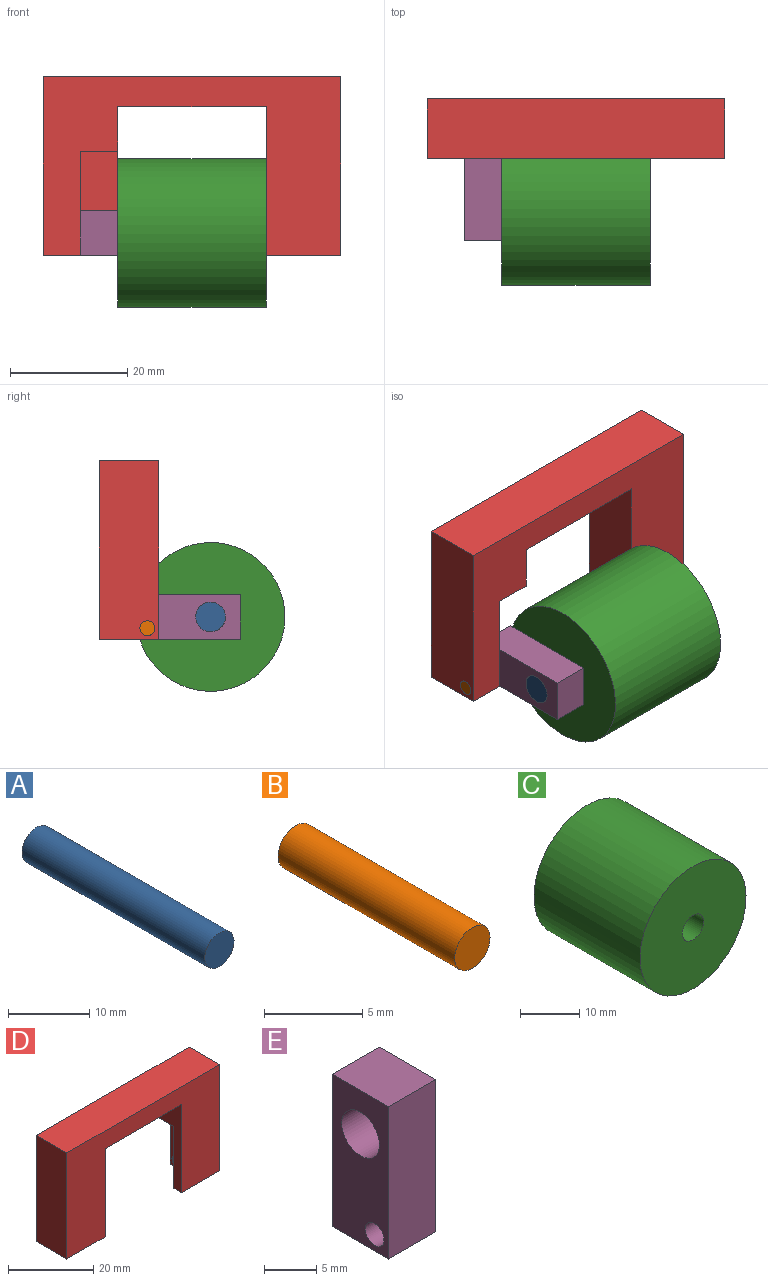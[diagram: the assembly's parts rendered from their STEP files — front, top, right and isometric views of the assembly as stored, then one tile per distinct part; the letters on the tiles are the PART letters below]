
ASSEMBLY  parts=5 mates=4
PART A: 3 faces, bbox 5.1x31.8x5.1 mm
  f0: cylinder r=2.54mm len=31.75mm, axis (0,1,0), area 506.7mm2, adj f1,f2
  f1: plane 5.08x5.08mm, normal (0,-1,0), area 20.3mm2, adj f0
  f2: plane 5.08x5.08mm, normal (0,1,0), area 20.3mm2, adj f0
PART B: 3 faces, bbox 2.5x12.7x2.5 mm
  f0: cylinder r=1.27mm len=12.7mm, axis (0,1,0), area 101.3mm2, adj f1,f2
  f1: plane 2.54x2.54mm, normal (0,-1,0), area 5.1mm2, adj f0
  f2: plane 2.54x2.54mm, normal (0,1,0), area 5.1mm2, adj f0
PART C: 4 faces, bbox 25.4x25.4x25.4 mm
  f0: cylinder r=12.7mm len=25.4mm, axis (0,1,0), area 2026.8mm2, adj f1,f2
  f1: plane 25.4x25.4mm, normal (0,-1,0), area 486.4mm2, adj f0,f3
  f2: plane 25.4x25.4mm, normal (0,1,0), area 486.4mm2, adj f0,f3
  f3: cylinder r=2.54mm len=25.4mm, axis (0,-1,0), area 405.4mm2, adj f1,f2
PART D: 14 faces, bbox 50.8x10.2x30.5 mm
  f0: plane 50.8x30.48mm, normal (0,1,0), area 790.3mm2, adj f1,f2,f3,f4,f5,f6,f7,f8
  f1: plane 25.4x10.16mm, normal (-1,0,0), area 122.6mm2, adj f0,f2,f8,f9,f10,f12
  f2: plane 12.7x10.16mm, normal (0,0,-1), area 80.6mm2, adj f0,f1,f3,f9,f11,f12
  f3: plane 30.48x10.16mm, normal (1,0,0), area 304.6mm2, adj f0,f2,f4,f9,f13
  f4: plane 50.8x10.16mm, normal (0,0,1), area 516.1mm2, adj f0,f3,f5,f9
  f5: plane 30.48x10.16mm, normal (-1,0,0), area 309.7mm2, adj f0,f4,f6,f9
  f6: plane 12.7x10.16mm, normal (0,0,-1), area 129mm2, adj f0,f5,f7,f9
  f7: plane 25.4x10.16mm, normal (1,0,0), area 258.1mm2, adj f0,f6,f8,f9
  f8: plane 25.4x10.16mm, normal (0,0,-1), area 258.1mm2, adj f0,f1,f7,f9
  f9: plane 50.8x30.48mm, normal (0,-1,0), area 903.2mm2, adj f1,f2,f3,f4,f5,f6,f7,f8
  f10: plane 7.62x6.35mm, normal (0,0,-1), area 48.4mm2, adj f0,f1,f11,f12
  f11: plane 17.78x7.62mm, normal (-1,0,0), area 130.4mm2, adj f0,f2,f10,f12,f13
  f12: plane 17.78x6.35mm, normal (0,1,0), area 112.9mm2, adj f1,f2,f10,f11
  f13: cylinder r=1.27mm len=6.35mm, axis (1,0,0), area 50.7mm2, adj f3,f11
PART E: 8 faces, bbox 6.4x7.6x17.8 mm
  f0: plane 17.78x7.62mm, normal (-1,0,0), area 110.1mm2, adj f1,f3,f4,f5,f6,f7
  f1: plane 7.62x6.35mm, normal (0,0,-1), area 48.4mm2, adj f0,f2,f4,f5
  f2: plane 17.78x7.62mm, normal (1,0,0), area 110.1mm2, adj f1,f3,f4,f5,f6,f7
  f3: plane 7.62x6.35mm, normal (0,0,1), area 48.4mm2, adj f0,f2,f4,f5
  f4: plane 17.78x6.35mm, normal (0,1,0), area 112.9mm2, adj f0,f1,f2,f3
  f5: plane 17.78x6.35mm, normal (0,-1,0), area 112.9mm2, adj f0,f1,f2,f3
  f6: cylinder r=1.27mm len=6.35mm, axis (1,0,0), area 50.7mm2, adj f0,f2
  f7: cylinder r=2.54mm len=6.35mm, axis (1,0,0), area 101.3mm2, adj f0,f2
PLACE A rot(axis=(0,0,1),90deg) t=(-49.83,-36.79,26.58)mm
PLACE B rot(axis=(0,0,-1),90deg) t=(-43.48,-26,24.67)mm
PLACE C rot(axis=(-0.6,0.6,0.53),123.7deg) t=(-43.48,-36.79,26.58)mm
PLACE D rot(axis=(0,0,1),180deg) t=(-5.38,-27.9,22.77)mm fixed
PLACE E rot(axis=(1,0,0),90deg) t=(-49.83,-24.09,22.77)mm
MATE fastened A.f0 <-> E.f7  axis (-1,0,0) through (-49.83,-36.79,26.58)mm
MATE fastened B.f0 <-> D.f13  axis (-1,0,0) through (-56.18,-26,24.67)mm
MATE revolute E.f6 <-> D.f13  axis (-1,0,0) through (-49.83,-26,24.67)mm
MATE revolute C.f3 <-> E.f7  axis (-1,0,0) through (-43.48,-36.79,26.58)mm
